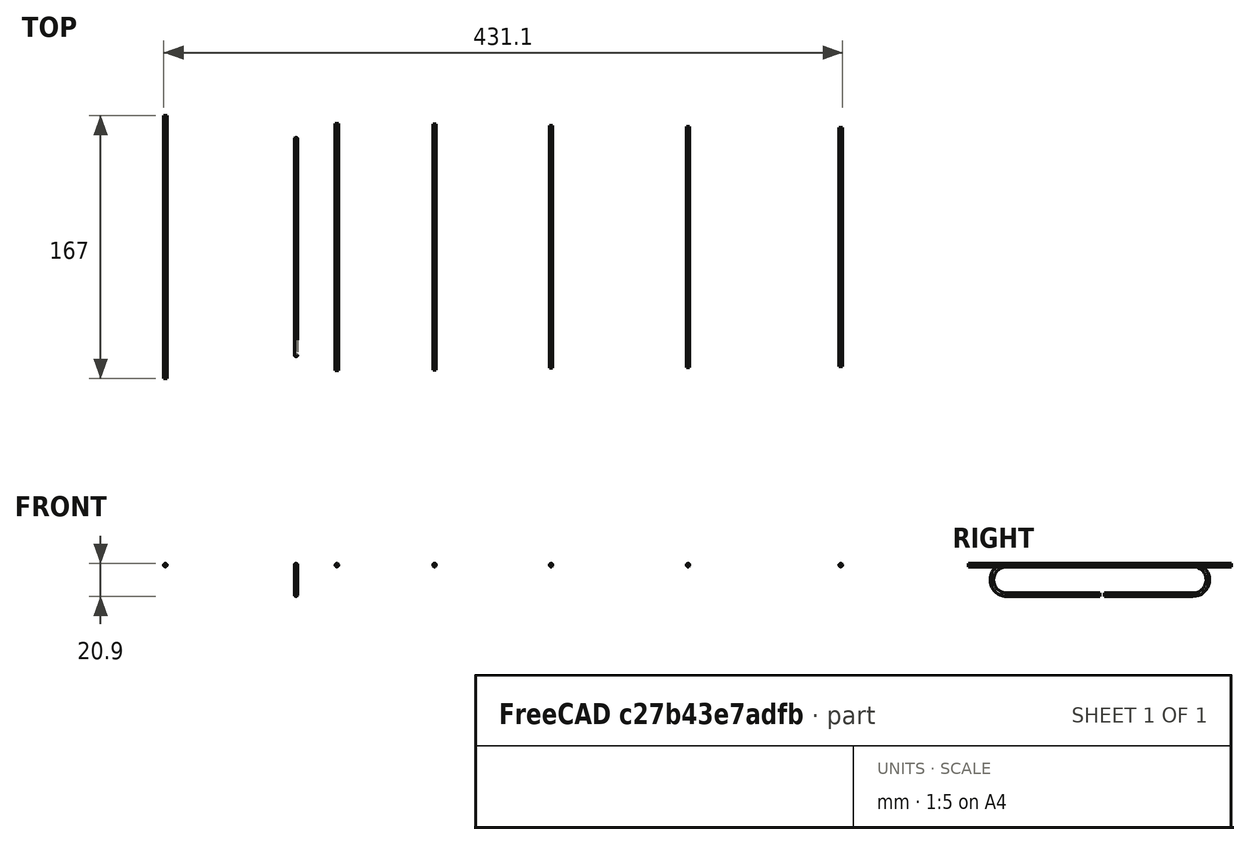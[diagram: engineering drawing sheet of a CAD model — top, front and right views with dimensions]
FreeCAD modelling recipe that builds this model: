
FCSTD DOCUMENT  (FreeCAD 0.19R24366 (Git))
Label: yagi
License: Creative Commons Attribution-ShareAlike
LicenseURL: http://creativecommons.org/licenses/by-sa/4.0/
objects: TechDraw::DrawViewDimension×17, Sketcher::SketchObject×8, TechDraw::DrawViewBalloon×8, PartDesign::Body×7, PartDesign::Pad×6, TechDraw::DrawSVGTemplate×3, TechDraw::DrawViewPart×3, TechDraw::DrawPage×3, TechDraw::DrawViewAnnotation×2, PartDesign::AdditivePipe×1
note: 29 computed .brp shape members not serialized (recipe doc carries the construction recipe); baked Part::Feature solids carry a one-line shape summary decoded from their .brp

FEATURE [Sketcher::SketchObject] Sketch  label="Reflector"
  FullyConstrained = true
  MapMode = 5
  Placement = pos=(0,0,0) rot=(1,0,0;1.5708rad)
  Support = -> [XZ_Plane]
  sketch-geometry (1):
    g0: Circle CenterX=0 CenterY=0 CenterZ=0 NormalX=0 NormalY=0 NormalZ=1 AngleXU=0 Radius=1.05
  constraints (2):
    c: Coincident(g0,g-1)
    c: Diameter(g0) = 2.1
FEATURE [PartDesign::Pad] Pad  label="reflector_Varilla"
  Direction = (1,1,1)
  Length = 167
  Length2 = 100
  Midplane = true
  Placement = pos=(0,0,0) rot=(1,0,0;1.5708rad)
  Profile = -> Sketch
  Type = 0
FEATURE [PartDesign::Body] Body  label="reflector"
  Group = -> [Sketch,Pad]
  Origin = -> Origin
  Tip = -> Pad
FEATURE [Sketcher::SketchObject] Sketch001
  FullyConstrained = true
  MapMode = 5
  Placement = pos=(0,0,0) rot=(1,0,0;1.5708rad)
  Support = -> [XZ_Plane001]
  sketch-geometry (1):
    g0: Circle CenterX=109 CenterY=0 CenterZ=0 NormalX=0 NormalY=0 NormalZ=1 AngleXU=0 Radius=1.05
  constraints (3):
    c: PointOnObject(g0,g-1)
    c: DistanceX(g-1,g0) = 109
    c: Diameter(g0) = 2.1
FEATURE [PartDesign::Pad] Pad001
  Direction = (1,1,1)
  Length = 157
  Length2 = 100
  Midplane = true
  Placement = pos=(0,0,0) rot=(1,0,0;1.5708rad)
  Profile = -> Sketch001
  Type = 0
FEATURE [PartDesign::Body] Body001  label="primer_director"
  Group = -> [Sketch001,Pad001]
  Origin = -> Origin001
  Tip = -> Pad001
FEATURE [Sketcher::SketchObject] Sketch002
  FullyConstrained = true
  MapMode = 5
  Placement = pos=(0,0,0) rot=(1,0,0;1.5708rad)
  Support = -> [XZ_Plane001]
  sketch-geometry (1):
    g0: Circle CenterX=171 CenterY=0 CenterZ=0 NormalX=0 NormalY=0 NormalZ=1 AngleXU=0 Radius=1.05
  constraints (3):
    c: PointOnObject(g0,g-1)
    c: DistanceX(g-1,g0) = 171
    c: Diameter(g0) = 2.1
FEATURE [PartDesign::Pad] Pad002
  Direction = (1,1,1)
  Length = 156
  Length2 = 100
  Midplane = true
  Placement = pos=(0,0,0) rot=(1,0,0;1.5708rad)
  Profile = -> Sketch002
  Type = 0
FEATURE [PartDesign::Body] Body002  label="segundo_director"
  Group = -> [Sketch002,Pad002]
  Origin = -> Origin002
  Tip = -> Pad002
FEATURE [Sketcher::SketchObject] Sketch003
  FullyConstrained = true
  MapMode = 5
  Placement = pos=(0,0,0) rot=(1,0,0;1.5708rad)
  sketch-geometry (1):
    g0: Circle CenterX=245 CenterY=0 CenterZ=0 NormalX=0 NormalY=0 NormalZ=1 AngleXU=0 Radius=1.05
  constraints (3):
    c: PointOnObject(g0,g-1)
    c: DistanceX(g-1,g0) = 245
    c: Diameter(g0) = 2.1
FEATURE [PartDesign::Pad] Pad003
  Direction = (1,1,1)
  Length = 154
  Length2 = 100
  Midplane = true
  Placement = pos=(0,0,0) rot=(1,0,0;1.5708rad)
  Profile = -> Sketch003
  Type = 0
FEATURE [PartDesign::Body] Body003  label="tercer_director"
  Group = -> [Sketch003,Pad003]
  Origin = -> Origin003
  Tip = -> Pad003
FEATURE [Sketcher::SketchObject] Sketch004
  FullyConstrained = true
  MapMode = 5
  Placement = pos=(0,0,0) rot=(1,0,0;1.5708rad)
  Support = -> [XZ_Plane001]
  sketch-geometry (1):
    g0: Circle CenterX=332 CenterY=0 CenterZ=0 NormalX=0 NormalY=0 NormalZ=1 AngleXU=0 Radius=1.05
  constraints (3):
    c: PointOnObject(g0,g-1)
    c: DistanceX(g-1,g0) = 332
    c: Diameter(g0) = 2.1
FEATURE [PartDesign::Pad] Pad004
  Direction = (1,1,1)
  Length = 153
  Length2 = 100
  Midplane = true
  Placement = pos=(0,0,0) rot=(1,0,0;1.5708rad)
  Profile = -> Sketch004
  Type = 0
FEATURE [PartDesign::Body] Body004  label="cuarto_director"
  Group = -> [Sketch004,Pad004]
  Origin = -> Origin004
  Tip = -> Pad004
FEATURE [Sketcher::SketchObject] Sketch005
  FullyConstrained = true
  MapMode = 5
  Placement = pos=(0,0,0) rot=(1,0,0;1.5708rad)
  Support = -> [XZ_Plane004]
  sketch-geometry (1):
    g0: Circle CenterX=429 CenterY=0 CenterZ=0 NormalX=0 NormalY=0 NormalZ=1 AngleXU=0 Radius=1.05
  constraints (3):
    c: PointOnObject(g0,g-1)
    c: DistanceX(g-1,g0) = 429
    c: Diameter(g0) = 2.1
FEATURE [PartDesign::Pad] Pad005
  Direction = (1,1,1)
  Length = 152
  Length2 = 100
  Midplane = true
  Placement = pos=(0,0,0) rot=(1,0,0;1.5708rad)
  Profile = -> Sketch005
  Type = 0
FEATURE [PartDesign::Body] Body005  label="quinto_director"
  Group = -> [Sketch005,Pad005]
  Origin = -> Origin005
  Tip = -> Pad005
FEATURE [Sketcher::SketchObject] Sketch006  label="dipolo"
  AttachmentOffset = pos=(0,0,83) rot=(0,0,1;0rad)
  FullyConstrained = true
  MapMode = 5
  Placement = pos=(83,-1.84e-14,1.84e-14) rot=(0.57735,0.57735,0.57735;2.0944rad)
  Support = -> [YZ_Plane006]
  sketch-geometry (5):
    g0: ArcOfCircle CenterX=-59.2 CenterY=-9.4 CenterZ=0 NormalX=0 NormalY=0 NormalZ=1 AngleXU=0 Radius=9.4 StartAngle=1.5708 EndAngle=4.71239
    g1: ArcOfCircle CenterX=59.2 CenterY=-9.4 CenterZ=0 NormalX=0 NormalY=0 NormalZ=1 AngleXU=0 Radius=9.4 StartAngle=4.71239 EndAngle=7.85398
    g2: LineSegment StartX=-59.2 StartY=-18.8 StartZ=0 EndX=0 EndY=-18.8 EndZ=0
    g3: LineSegment StartX=-59.2 StartY=0 StartZ=0 EndX=59.2 EndY=0 EndZ=0
    g4: LineSegment StartX=59.2 StartY=-18.8 StartZ=0 EndX=2.9 EndY=-18.8 EndZ=0
  constraints (14):
    c: Tangent(g0,g3) = 1.5708
    c: Tangent(g0,g2) = -1.5708
    c: Tangent(g3,g1) = 1.5708
    c: Horizontal(g2)
    c: PointOnObject(g1,g-1)
    c: Symmetric(g0,g1,g-2)
    c: DistanceX(g3,g3) = 118.4
    c: Radius(g1) = 9.4
    c: Equal(g0,g1)
    c: DistanceX(g2,g2) = 59.2
    c: Coincident(g4,g1)
    c: Horizontal(g4)
    c: DistanceX(g4,g4) = 56.3
    c: PointOnObject(g4,g2)
FEATURE [Sketcher::SketchObject] Sketch007  label="seccion"
  FullyConstrained = false
  Placement = pos=(15.7451,2.9,-20.313) rot=(1,0,0;1.5708rad)
  sketch-geometry (1):
    g0: Circle CenterX=67.2549 CenterY=1.51305 CenterZ=0 NormalX=0 NormalY=0 NormalZ=1 AngleXU=0 Radius=1.05
  constraints (1):
    c: Diameter(g0) = 2.1
FEATURE [PartDesign::AdditivePipe] AdditivePipe
  AuxilleryCurvelinear = true
  AuxillerySpineTangent = false
  Binormal = (0,0,0)
  Mode = 0
  Placement = pos=(15.7451,2.9,-20.313) rot=(1,0,0;1.5708rad)
  Profile = -> Sketch007
  Spine = -> Sketch006
  SpineTangent = false
  Transformation = 0
  Transition = 0
FEATURE [PartDesign::Body] Body006  label="dipolo_cuerpo"
  Group = -> [Sketch006,Sketch007,AdditivePipe]
  Origin = -> Origin006
  Tip = -> AdditivePipe
FEATURE [TechDraw::DrawSVGTemplate] Template
  Height = 210
  Orientation = 1
  Width = 297
FEATURE [TechDraw::DrawViewPart] View
  CoarseView = false
  Direction = (0,0,1)
  Focus = 100
  HardHidden = false
  IsoCount = 0
  IsoHidden = false
  IsoVisible = false
  LockPosition = false
  Perspective = false
  Rotation = 0
  ScaleType = 0
  SeamHidden = false
  SeamVisible = true
  SmoothHidden = false
  SmoothVisible = true
  Source = -> [Body006,Body,Body001,Body002,Body003]
  X = 148.255
  XDirection = (1,0,0)
  Y = 105
FEATURE [TechDraw::DrawViewDimension] Dimension
  Arbitrary = false
  ArbitraryTolerances = false
  EqualTolerance = true
  FormatSpec = %.2f
  FormatSpecOverTolerance = %+.2f
  FormatSpecUnderTolerance = %+.2f
  Inverted = false
  LockPosition = false
  MeasureType = 1
  OverTolerance = 0
  References2D = -> [View]
  Rotation = 0
  ScaleType = 0
  TheoreticalExact = false
  Type = 1
  UnderTolerance = 0
  X = -80.6861
  Y = 91.2619
FEATURE [TechDraw::DrawViewDimension] Dimension001
  Arbitrary = false
  ArbitraryTolerances = false
  EqualTolerance = true
  FormatSpec = %.2f
  FormatSpecOverTolerance = %+.2f
  FormatSpecUnderTolerance = %+.2f
  Inverted = false
  LockPosition = false
  MeasureType = 1
  OverTolerance = 0
  References2D = -> [View]
  Rotation = 0
  ScaleType = 0
  TheoreticalExact = false
  Type = 1
  UnderTolerance = 0
  X = -55.7244
  Y = 99.6422
FEATURE [TechDraw::DrawViewDimension] Dimension002
  Arbitrary = false
  ArbitraryTolerances = false
  EqualTolerance = true
  FormatSpec = %.2f
  FormatSpecOverTolerance = %+.2f
  FormatSpecUnderTolerance = %+.2f
  Inverted = false
  LockPosition = false
  MeasureType = 1
  OverTolerance = 0
  References2D = -> [View]
  Rotation = 0
  ScaleType = 0
  TheoreticalExact = false
  Type = 1
  UnderTolerance = 0
  X = 16.1982
  Y = 91.3526
FEATURE [TechDraw::DrawViewDimension] Dimension003
  Arbitrary = false
  ArbitraryTolerances = false
  EqualTolerance = true
  FormatSpec = %.2f
  FormatSpecOverTolerance = %+.2f
  FormatSpecUnderTolerance = %+.2f
  Inverted = false
  LockPosition = false
  MeasureType = 1
  OverTolerance = 0
  References2D = -> [View]
  Rotation = 0
  ScaleType = 0
  TheoreticalExact = false
  Type = 1
  UnderTolerance = 0
  X = 85.6667
  Y = 91.1907
FEATURE [TechDraw::DrawViewDimension] Dimension004
  Arbitrary = false
  ArbitraryTolerances = false
  EqualTolerance = true
  FormatSpec = %.2f
  FormatSpecOverTolerance = %+.2f
  FormatSpecUnderTolerance = %+.2f
  Inverted = false
  LockPosition = false
  MeasureType = 1
  OverTolerance = 0
  References2D = -> [View]
  Rotation = 0
  ScaleType = 0
  TheoreticalExact = false
  Type = 2
  UnderTolerance = 0
  X = -114.428
  Y = 0
FEATURE [TechDraw::DrawViewDimension] Dimension005
  Arbitrary = false
  ArbitraryTolerances = false
  EqualTolerance = true
  FormatSpec = %.2f
  FormatSpecOverTolerance = %+.2f
  FormatSpecUnderTolerance = %+.2f
  Inverted = false
  LockPosition = false
  MeasureType = 1
  OverTolerance = 0
  References2D = -> [View]
  Rotation = 0
  ScaleType = 0
  TheoreticalExact = false
  Type = 2
  UnderTolerance = 0
  X = 2.26338
  Y = 0
FEATURE [TechDraw::DrawViewDimension] Dimension006
  Arbitrary = false
  ArbitraryTolerances = false
  EqualTolerance = true
  FormatSpec = %.2f
  FormatSpecOverTolerance = %+.2f
  FormatSpecUnderTolerance = %+.2f
  Inverted = false
  LockPosition = false
  MeasureType = 1
  OverTolerance = 0
  References2D = -> [View]
  Rotation = 0
  ScaleType = 0
  TheoreticalExact = false
  Type = 2
  UnderTolerance = 0
  X = 60.9194
  Y = 0
FEATURE [TechDraw::DrawViewDimension] Dimension007
  Arbitrary = false
  ArbitraryTolerances = false
  EqualTolerance = true
  FormatSpec = %.2f
  FormatSpecOverTolerance = %+.2f
  FormatSpecUnderTolerance = %+.2f
  Inverted = false
  LockPosition = false
  MeasureType = 1
  OverTolerance = 0
  References2D = -> [View]
  Rotation = 0
  ScaleType = 0
  TheoreticalExact = false
  Type = 2
  UnderTolerance = 0
  X = 132.244
  Y = -0.66879
FEATURE [TechDraw::DrawViewBalloon] Balloon
  BubbleShape = 0
  EndType = 0
  EndTypeScale = 1
  KinkLength = 5
  LockPosition = false
  OriginX = -124.1
  OriginY = 41.9277
  Rotation = 0
  ScaleType = 0
  ShapeScale = 1
  SourceView = -> View
  Text = 1
  TextWrapLen = -1
  X = -91.2595
  Y = 52.6984
FEATURE [TechDraw::DrawViewBalloon] Balloon001
  BubbleShape = 0
  EndType = 0
  EndTypeScale = 1
  KinkLength = 5
  LockPosition = false
  OriginX = -39.4315
  OriginY = 23.8704
  Rotation = 0
  ScaleType = 0
  ShapeScale = 1
  SourceView = -> View
  Text = 2
  TextWrapLen = -1
  X = -76.0111
  Y = 33.8386
FEATURE [TechDraw::DrawViewBalloon] Balloon002
  BubbleShape = 0
  EndType = 0
  EndTypeScale = 1
  KinkLength = 5
  LockPosition = false
  OriginX = -14.5525
  OriginY = 14.2398
  Rotation = 0
  ScaleType = 0
  ShapeScale = 1
  SourceView = -> View
  Text = 3
  TextWrapLen = -1
  X = -28.6608
  Y = -6.28883
FEATURE [TechDraw::DrawViewBalloon] Balloon003
  BubbleShape = 0
  EndType = 0
  EndTypeScale = 1
  KinkLength = 5
  LockPosition = false
  OriginX = 46.4411
  OriginY = 9.82582
  Rotation = 0
  ScaleType = 0
  ShapeScale = 1
  SourceView = -> View
  Text = 4
  TextWrapLen = -1
  X = 27.1163
  Y = 22.2016
FEATURE [TechDraw::DrawViewBalloon] Balloon004
  BubbleShape = 0
  EndType = 0
  EndTypeScale = 1
  KinkLength = 5
  LockPosition = false
  OriginX = 121.881
  OriginY = -5.02132
  Rotation = 0
  ScaleType = 0
  ShapeScale = 1
  SourceView = -> View
  Text = 5
  TextWrapLen = -1
  X = 96.9379
  Y = 14.9787
FEATURE [TechDraw::DrawViewAnnotation] Annotation
  Font = DejaVu Sans
  LineSpace = 80
  LockPosition = false
  MaxWidth = -1
  Rotation = 0
  ScaleType = 0
  Text = 1) Reflector | 2) Dipolo | 3) primer director | 4) segundo director | 5) tercer director
  TextSize = 4
  TextStyle = 0
  X = 69.8503
  Y = 54.8408
FEATURE [TechDraw::DrawPage] Page  label="primera parte"
  KeepUpdated = true
  NextBalloonIndex = 6
  ProjectionType = 0
  Template = -> Template
  Views = -> [View,Dimension,Dimension001,Dimension002,Dimension003,Dimension004,Dimension005,Dimension006,Dimension007,Balloon,Balloon001,Balloon002,Balloon003,Balloon004,Annotation]
FEATURE [TechDraw::DrawSVGTemplate] Template001
  Height = 210
  Orientation = 1
  Width = 297
FEATURE [TechDraw::DrawViewPart] View001
  CoarseView = false
  Direction = (0,0,1)
  Focus = 100
  HardHidden = false
  IsoCount = 0
  IsoHidden = false
  IsoVisible = false
  LockPosition = false
  Perspective = false
  Rotation = 0
  ScaleType = 0
  SeamHidden = false
  SeamVisible = true
  SmoothHidden = false
  SmoothVisible = true
  Source = -> [Body003,Body004,Body005]
  X = 148.5
  XDirection = (1,0,0)
  Y = 105
FEATURE [TechDraw::DrawViewDimension] Dimension008
  Arbitrary = false
  ArbitraryTolerances = false
  EqualTolerance = true
  FormatSpec = %.2f
  FormatSpecOverTolerance = %+.2f
  FormatSpecUnderTolerance = %+.2f
  Inverted = false
  LockPosition = false
  MeasureType = 1
  OverTolerance = 0
  References2D = -> [View001]
  Rotation = 0
  ScaleType = 0
  TheoreticalExact = false
  Type = 1
  UnderTolerance = 0
  X = -48.5699
  Y = 85.1491
FEATURE [TechDraw::DrawViewDimension] Dimension009
  Arbitrary = false
  ArbitraryTolerances = false
  EqualTolerance = true
  FormatSpec = %.2f
  FormatSpecOverTolerance = %+.2f
  FormatSpecUnderTolerance = %+.2f
  Inverted = false
  LockPosition = false
  MeasureType = 1
  OverTolerance = 0
  References2D = -> [View001]
  Rotation = 0
  ScaleType = 0
  TheoreticalExact = false
  Type = 1
  UnderTolerance = 0
  X = 43.221
  Y = 85.0418
FEATURE [TechDraw::DrawViewDimension] Dimension010
  Arbitrary = false
  ArbitraryTolerances = false
  EqualTolerance = true
  FormatSpec = %.2f
  FormatSpecOverTolerance = %+.2f
  FormatSpecUnderTolerance = %+.2f
  Inverted = false
  LockPosition = false
  MeasureType = 1
  OverTolerance = 0
  References2D = -> [View001]
  Rotation = 0
  ScaleType = 0
  TheoreticalExact = false
  Type = 2
  UnderTolerance = 0
  X = -77.3965
  Y = -1.46524
FEATURE [TechDraw::DrawViewDimension] Dimension011
  Arbitrary = false
  ArbitraryTolerances = false
  EqualTolerance = true
  FormatSpec = %.2f
  FormatSpecOverTolerance = %+.2f
  FormatSpecUnderTolerance = %+.2f
  Inverted = false
  LockPosition = false
  MeasureType = 1
  OverTolerance = 0
  References2D = -> [View001]
  Rotation = 0
  ScaleType = 0
  TheoreticalExact = false
  Type = 2
  UnderTolerance = 0
  X = 10.7025
  Y = -1.09893
FEATURE [TechDraw::DrawViewDimension] Dimension012
  Arbitrary = false
  ArbitraryTolerances = false
  EqualTolerance = true
  FormatSpec = %.2f
  FormatSpecOverTolerance = %+.2f
  FormatSpecUnderTolerance = %+.2f
  Inverted = false
  LockPosition = false
  MeasureType = 1
  OverTolerance = 0
  References2D = -> [View001]
  Rotation = 0
  ScaleType = 0
  TheoreticalExact = false
  Type = 2
  UnderTolerance = 0
  X = 102.94
  Y = 0
FEATURE [TechDraw::DrawViewBalloon] Balloon005
  BubbleShape = 3
  EndType = 0
  EndTypeScale = 1
  KinkLength = 5
  LockPosition = false
  OriginX = -93.412
  OriginY = 20.6102
  Rotation = 0
  ScaleType = 0
  ShapeScale = 1
  SourceView = -> View001
  Text = Tercer director
  TextWrapLen = -1
  X = -50.3344
  Y = 53.7974
FEATURE [TechDraw::DrawViewBalloon] Balloon006
  BubbleShape = 3
  EndType = 0
  EndTypeScale = 1
  KinkLength = 5
  LockPosition = false
  OriginX = -5.49732
  OriginY = 14.0166
  Rotation = 0
  ScaleType = 0
  ShapeScale = 1
  SourceView = -> View001
  Text = cuarto director
  TextWrapLen = -1
  X = -45.9387
  Y = 25.9578
FEATURE [TechDraw::DrawViewBalloon] Balloon007
  BubbleShape = 3
  EndType = 0
  EndTypeScale = 1
  KinkLength = 5
  LockPosition = false
  OriginX = 90.1099
  OriginY = 3.75991
  Rotation = 0
  ScaleType = 0
  ShapeScale = 1
  SourceView = -> View001
  Text = quinto director
  TextWrapLen = -1
  X = 47.837
  Y = 19.3642
FEATURE [TechDraw::DrawPage] Page001  label="segunda_parte"
  KeepUpdated = true
  NextBalloonIndex = 4
  ProjectionType = 0
  Template = -> Template001
  Views = -> [View001,Dimension008,Dimension009,Dimension010,Dimension011,Dimension012,Balloon005,Balloon006,Balloon007]
FEATURE [TechDraw::DrawSVGTemplate] Template002
  Height = 210
  Orientation = 1
  Width = 297
FEATURE [TechDraw::DrawViewPart] View002
  CoarseView = false
  Direction = (1,0,0)
  Focus = 100
  HardHidden = false
  IsoCount = 0
  IsoHidden = false
  IsoVisible = false
  LockPosition = false
  Perspective = false
  Rotation = 0
  ScaleType = 0
  SeamHidden = false
  SeamVisible = true
  SmoothHidden = false
  SmoothVisible = true
  Source = -> [Template002,Body006]
  X = 149.615
  XDirection = (0,1,0)
  Y = 105.836
FEATURE [TechDraw::DrawViewDimension] Dimension013
  Arbitrary = false
  ArbitraryTolerances = false
  EqualTolerance = true
  FormatSpec = %.2f
  FormatSpecOverTolerance = %+.2f
  FormatSpecUnderTolerance = %+.2f
  Inverted = false
  LockPosition = false
  MeasureType = 1
  OverTolerance = 0
  References2D = -> [View002]
  Rotation = 0
  ScaleType = 0
  TheoreticalExact = false
  Type = 1
  UnderTolerance = 0
  X = -1.47212
  Y = 28.5571
FEATURE [TechDraw::DrawViewDimension] Dimension014
  Arbitrary = false
  ArbitraryTolerances = false
  EqualTolerance = true
  FormatSpec = %.2f
  FormatSpecOverTolerance = %+.2f
  FormatSpecUnderTolerance = %+.2f
  Inverted = false
  LockPosition = false
  MeasureType = 1
  OverTolerance = 0
  References2D = -> [View002]
  Rotation = 0
  ScaleType = 0
  TheoreticalExact = false
  Type = 1
  UnderTolerance = 0
  X = 31.05
  Y = -17.6634
FEATURE [TechDraw::DrawViewDimension] Dimension015
  Arbitrary = false
  ArbitraryTolerances = false
  EqualTolerance = true
  FormatSpec = %.2f
  FormatSpecOverTolerance = %+.2f
  FormatSpecUnderTolerance = %+.2f
  Inverted = false
  LockPosition = false
  MeasureType = 1
  OverTolerance = 0
  References2D = -> [View002]
  Rotation = 0
  ScaleType = 0
  TheoreticalExact = false
  Type = 1
  UnderTolerance = 0
  X = -28.4223
  Y = -17.9578
FEATURE [TechDraw::DrawViewDimension] Dimension016
  Arbitrary = false
  ArbitraryTolerances = false
  EqualTolerance = true
  FormatSpec = R%.2f
  FormatSpecOverTolerance = %+.2f
  FormatSpecUnderTolerance = %+.2f
  Inverted = false
  LockPosition = false
  MeasureType = 1
  OverTolerance = 0
  References2D = -> [View002]
  Rotation = 0
  ScaleType = 0
  TheoreticalExact = false
  Type = 4
  UnderTolerance = 0
  X = -83.7638
  Y = 12.2186
FEATURE [TechDraw::DrawViewAnnotation] Annotation001
  Font = DejaVu Sans
  LineSpace = 80
  LockPosition = false
  MaxWidth = -1
  Rotation = 0
  ScaleType = 0
  Text = Longitud total 296.1 mm
  TextSize = 4
  TextStyle = 0
  X = 150.451
  Y = 68.7739
FEATURE [TechDraw::DrawPage] Page002  label="dibujo_dipolo"
  KeepUpdated = true
  NextBalloonIndex = 1
  ProjectionType = 0
  Template = -> Template002
  Views = -> [View002,Dimension013,Dimension014,Dimension015,Dimension016,Annotation001]
